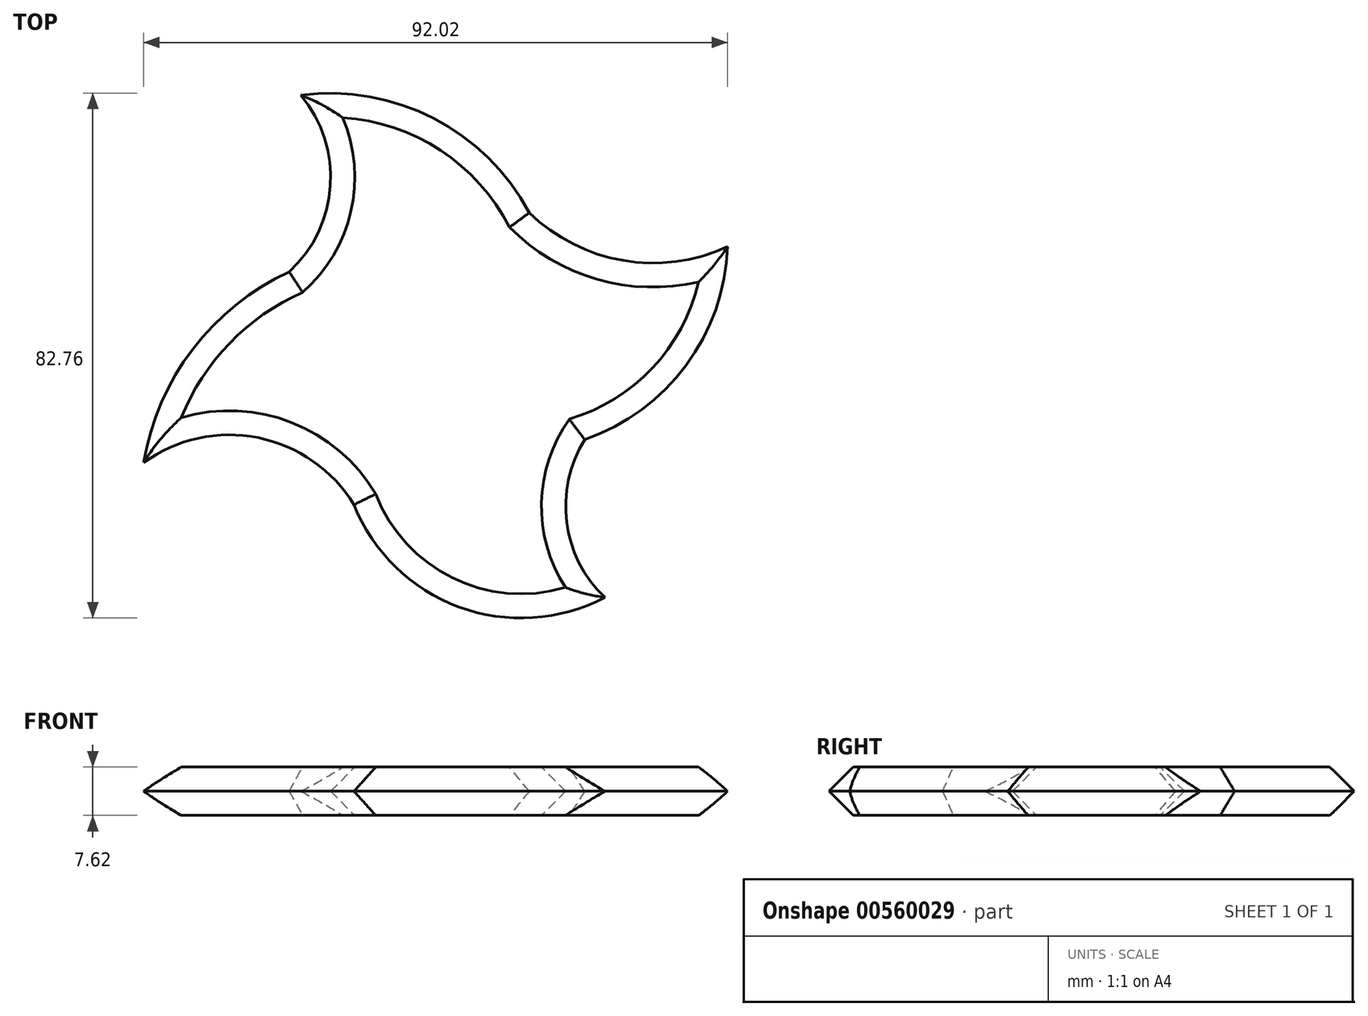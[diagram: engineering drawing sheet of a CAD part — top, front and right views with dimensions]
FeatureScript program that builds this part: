
annotation { "Feature Type Name" : "Feature", "Feature Type Description" : "" }
export const myFeature = defineFeature(function(context is Context, id is Id, definition is map)
    precondition{}
    {
        {
            var Q0;
            Q0=qCreatedBy(makeId("Top.planeOp"),FACE);
            var sketch = newSketch(context, id + "F0", { "sketchPlane" : qUnion([Q0])});
            skCircle(sketch, "E0.cCircle", {"center": v(0, 0) * mm, "radius": 28 * mm, "construction": true});
            skLineSegment(sketch, "E0.0", {"start": v(14.28, 24.08) * mm, "end": v(15.47, 23.37) * mm});
            skPoint(sketch, "E0.0.midPoint", {"position": v(14.28, 24.08) * mm});
            skPoint(sketch, "E1.orphan", {"position": v(-9.8, 38.35) * mm});
            skArc(sketch, "E2", {"start": v(-24.08, 14.28) * mm, "mid": v(-18.1, 28.12) * mm, "end": v(-24.08, 41.96) * mm});
            skArc(sketch, "E3", {"start": v(15.5, 23.3) * mm, "mid": v(-1.22, 39.15) * mm, "end": v(-24.08, 41.96) * mm});
            skPoint(sketch, "E4.orphan", {"position": v(9.8, -38.35) * mm});
            skArc(sketch, "E5", {"start": v(24.08, -14.28) * mm, "mid": v(21.8, -27.16) * mm, "end": v(28.59, -38.34) * mm});
            skArc(sketch, "E6", {"start": v(-14.28, -24.08) * mm, "mid": v(3.86, -41.12) * mm, "end": v(28.59, -38.34) * mm});
            skPoint(sketch, "E0.1.start.orphan", {"position": v(38.35, 9.8) * mm});
            skArc(sketch, "E7", {"start": v(-14.28, -24.08) * mm, "mid": v(-30.5, -13.88) * mm, "end": v(-48.5, -20.46) * mm});
            skArc(sketch, "E8", {"start": v(-24.08, 14.28) * mm, "mid": v(-40.6, 0.39) * mm, "end": v(-47.95, -19.9) * mm});
            skArc(sketch, "E9", {"start": v(15.5, 23.3) * mm, "mid": v(30.59, 16.1) * mm, "end": v(47, 19.25) * mm});
            skArc(sketch, "E10", {"start": v(24.08, -14.28) * mm, "mid": v(40.97, -1.23) * mm, "end": v(47, 19.25) * mm});
            skSolve(sketch);
        }
        {
            var Q0;
            Q0 = qSketchRegion(id + "F0", true);
            extrude(context, id + "F1", {"entities" : qUnion([Q0]), "depth" : 7.62 * mm, "offsetDistance" : 25.4 * mm});
        }
        {
            var Q0;
            Q0=makeQuery(id+"F1.opExtrude","CAP_EDGE",EDGE,{"disambiguationData":[OSD([sQuery(id+"F0.wireOp",EDGE,"E7")])],"isStart":false});
            var Q1;
            Q1=makeQuery(id+"F1.opExtrude","CAP_EDGE",EDGE,{"disambiguationData":[OSD([sQuery(id+"F0.wireOp",EDGE,"E6")])],"isStart":false});
            var Q2;
            Q2=makeQuery(id+"F1.opExtrude","CAP_EDGE",EDGE,{"disambiguationData":[OSD([sQuery(id+"F0.wireOp",EDGE,"E5")])],"isStart":false});
            var Q3;
            Q3=makeQuery(id+"F1.opExtrude","CAP_EDGE",EDGE,{"disambiguationData":[OSD([sQuery(id+"F0.wireOp",EDGE,"E10")])],"isStart":false});
            var Q4;
            Q4=makeQuery(id+"F1.opExtrude","CAP_EDGE",EDGE,{"disambiguationData":[OSD([sQuery(id+"F0.wireOp",EDGE,"E9")])],"isStart":false});
            var Q5;
            Q5=makeQuery(id+"F1.opExtrude","CAP_EDGE",EDGE,{"disambiguationData":[OSD([sQuery(id+"F0.wireOp",EDGE,"E3")])],"isStart":false});
            var Q6;
            Q6=makeQuery(id+"F1.opExtrude","CAP_EDGE",EDGE,{"disambiguationData":[OSD([sQuery(id+"F0.wireOp",EDGE,"E2")])],"isStart":false});
            var Q7;
            Q7=makeQuery(id+"F1.opExtrude","CAP_EDGE",EDGE,{"disambiguationData":[OSD([sQuery(id+"F0.wireOp",EDGE,"E8")])],"isStart":false});
            chamfer(context, id + "F2", {"entities" : qUnion([Q0, Q1, Q2, Q3, Q4, Q5, Q6, Q7]), "width" : 5.08 * mm, "tangentPropagation" : true});
        }
        {
            var Q0;
            Q0=makeQuery(id+"F1.opExtrude","CAP_EDGE",EDGE,{"disambiguationData":[OSD([sQuery(id+"F0.wireOp",EDGE,"E7")])],"isStart":true});
            var Q1;
            Q1=makeQuery(id+"F1.opExtrude","CAP_EDGE",EDGE,{"disambiguationData":[OSD([sQuery(id+"F0.wireOp",EDGE,"E6")])],"isStart":true});
            chamfer(context, id + "F3", {"entities" : qUnion([Q0, Q1]), "width" : 5.08 * mm, "tangentPropagation" : true});
        }
        {
            var Q0;
            Q0=makeQuery(id+"F1.opExtrude","CAP_EDGE",EDGE,{"disambiguationData":[OSD([sQuery(id+"F0.wireOp",EDGE,"E5")])],"isStart":true});
            var Q1;
            Q1=makeQuery(id+"F1.opExtrude","CAP_EDGE",EDGE,{"disambiguationData":[OSD([sQuery(id+"F0.wireOp",EDGE,"E10")])],"isStart":true});
            var Q2;
            Q2=makeQuery(id+"F1.opExtrude","CAP_EDGE",EDGE,{"disambiguationData":[OSD([sQuery(id+"F0.wireOp",EDGE,"E9")])],"isStart":true});
            var Q3;
            Q3=makeQuery(id+"F1.opExtrude","CAP_EDGE",EDGE,{"disambiguationData":[OSD([sQuery(id+"F0.wireOp",EDGE,"E3")])],"isStart":true});
            var Q4;
            Q4=makeQuery(id+"F1.opExtrude","CAP_EDGE",EDGE,{"disambiguationData":[OSD([sQuery(id+"F0.wireOp",EDGE,"E2")])],"isStart":true});
            var Q5;
            Q5=makeQuery(id+"F1.opExtrude","CAP_EDGE",EDGE,{"disambiguationData":[OSD([sQuery(id+"F0.wireOp",EDGE,"E8")])],"isStart":true});
            chamfer(context, id + "F4", {"entities" : qUnion([Q0, Q1, Q2, Q3, Q4, Q5]), "width" : 5.08 * mm, "tangentPropagation" : true});
        }
    });
